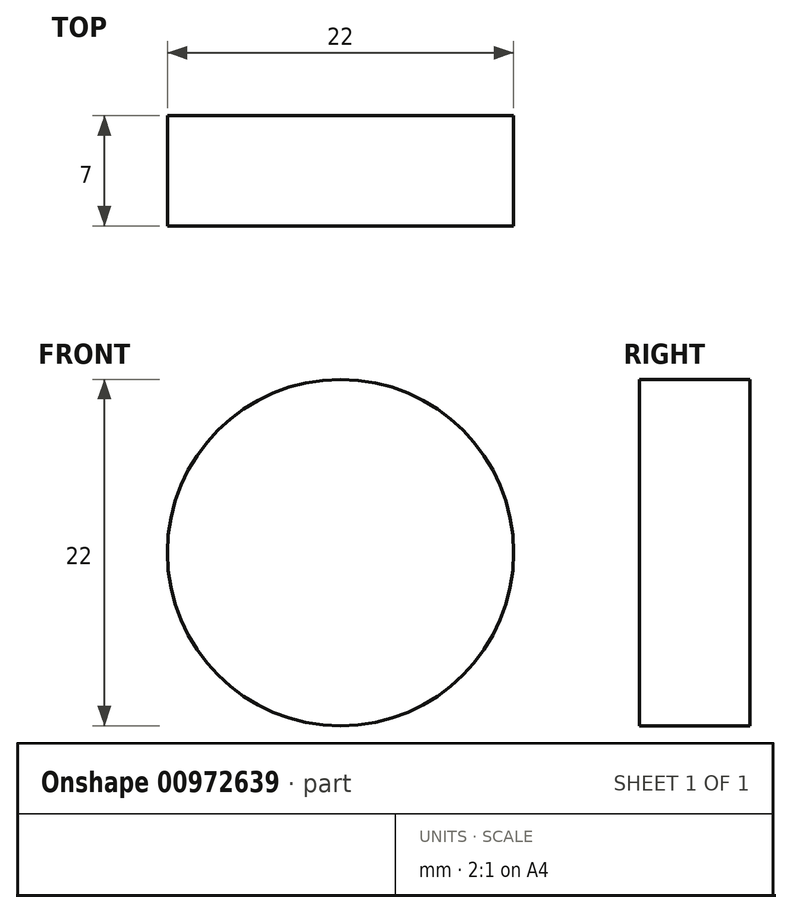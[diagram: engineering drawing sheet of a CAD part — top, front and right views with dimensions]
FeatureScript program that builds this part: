
annotation { "Feature Type Name" : "Feature", "Feature Type Description" : "" }
export const myFeature = defineFeature(function(context is Context, id is Id, definition is map)
    precondition{}
    {
        {
            var Q0;
            Q0=qCreatedBy(makeId("Front.planeOp"),FACE);
            var sketch = newSketch(context, id + "F0", { "sketchPlane" : qUnion([Q0])});
            skCircle(sketch, "E0", {"center": v(-46.56, 27.9) * mm, "radius": 11 * mm});
            skSolve(sketch);
        }
        {
            var Q0;
            Q0=makeQuery(id+"F0.imprint","IMPRINT",FACE,{"disambiguationData":[TD([[makeQuery(id+"F0.imprint","IMPRINT",EDGE,{"derivedFrom":sQuery(id+"F0.wireOp",EDGE,"E0")}),1.0]])]});
            extrude(context, id + "F1", {"entities" : qUnion([Q0]), "depth" : 7 * mm, "offsetDistance" : 25 * mm});
        }
    });
